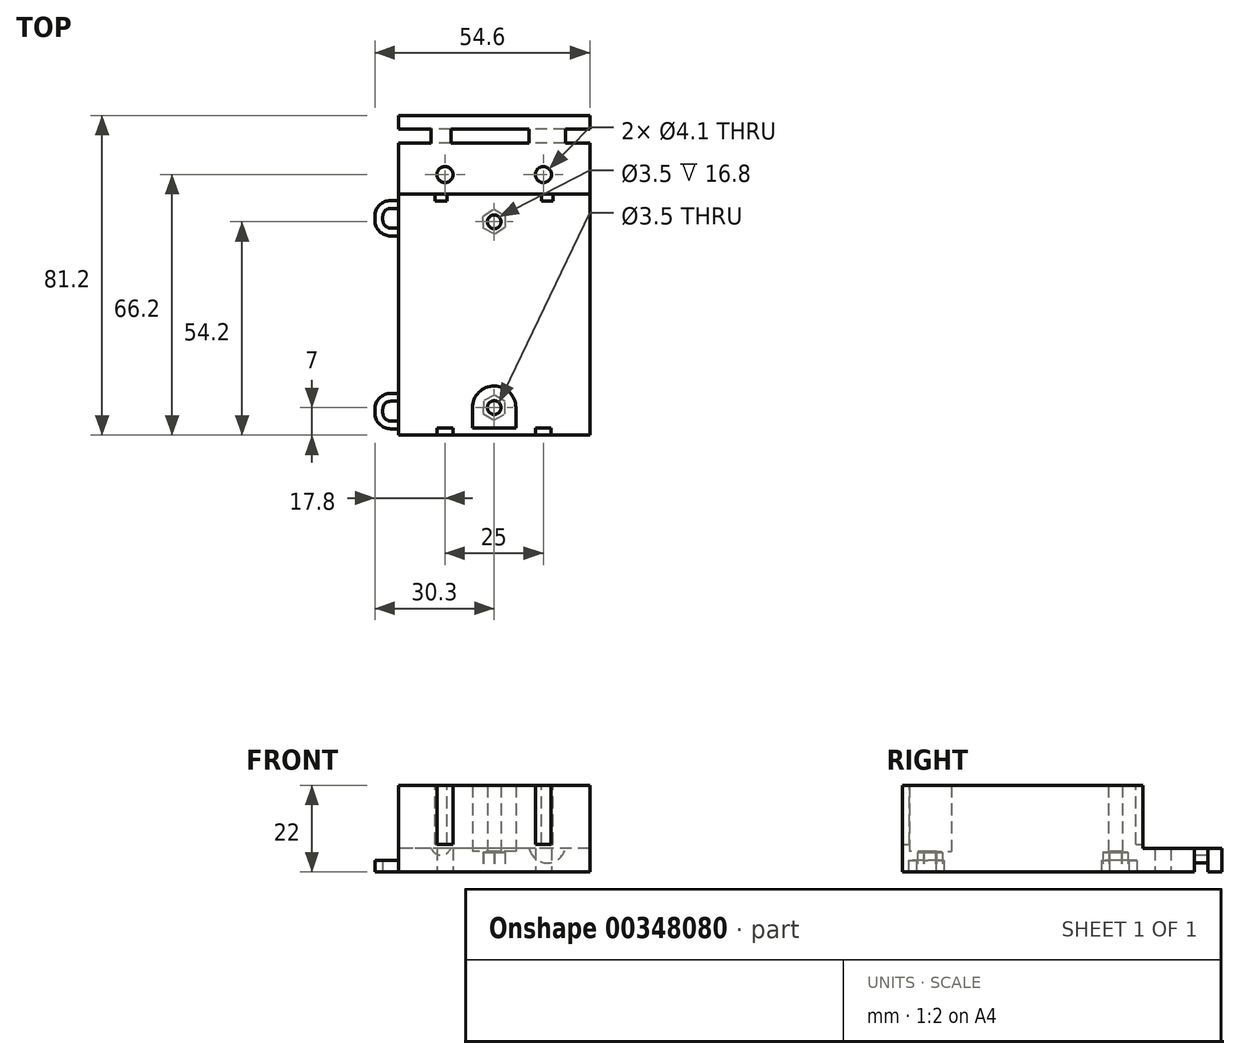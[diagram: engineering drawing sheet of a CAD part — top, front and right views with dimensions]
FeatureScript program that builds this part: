
annotation { "Feature Type Name" : "Feature", "Feature Type Description" : "" }
export const myFeature = defineFeature(function(context is Context, id is Id, definition is map)
    precondition{}
    {
        {
            var Q0;
            Q0=qCreatedBy(makeId("Top.planeOp"),FACE);
            var sketch = newSketch(context, id + "F0", { "sketchPlane" : qUnion([Q0])});
            skLineSegment(sketch, "E0.bottom", {"start": v(22.5, -28.8) * mm, "end": v(-22.5, -28.8) * mm});
            skLineSegment(sketch, "E0.top", {"start": v(22.5, 28.8) * mm, "end": v(-22.5, 28.8) * mm});
            skLineSegment(sketch, "E0.left", {"start": v(22.5, -28.8) * mm, "end": v(22.5, 28.8) * mm});
            skLineSegment(sketch, "E0.right", {"start": v(-22.5, -28.8) * mm, "end": v(-22.5, 28.8) * mm});
            skPoint(sketch, "E0.middle", {"position": v(0, 0) * mm});
            skLineSegment(sketch, "E1.bottom", {"start": v(24.3, -30.6) * mm, "end": v(-24.3, -30.6) * mm});
            skLineSegment(sketch, "E1.top", {"start": v(24.3, 50.6) * mm, "end": v(-24.3, 50.6) * mm});
            skLineSegment(sketch, "E1.left", {"start": v(24.3, -30.6) * mm, "end": v(24.3, 50.6) * mm});
            skLineSegment(sketch, "E1.right", {"start": v(-24.3, -30.6) * mm, "end": v(-24.3, 50.6) * mm});
            skPoint(sketch, "E1.middle", {"position": v(0, 10) * mm});
            skLineSegment(sketch, "E2", {"start": v(-24.3, 30.6) * mm, "end": v(24.3, 30.6) * mm});
            skPoint(sketch, "E3.startSnap0", {"position": v(-22.5, 0) * mm});
            skPoint(sketch, "E3.endSnap0", {"position": v(22.5, 0) * mm});
            skLineSegment(sketch, "E4", {"start": v(0, -30.6) * mm, "end": v(0, 50.6) * mm, "construction": true});
            skCircle(sketch, "E5", {"center": v(-12.5, 35.6) * mm, "radius": 2.05 * mm});
            skCircle(sketch, "E6.MirrorC", {"center": v(12.5, 35.6) * mm, "radius": 2.05 * mm});
            skCircle(sketch, "E7", {"center": v(0, 23.6) * mm, "radius": 1.75 * mm});
            skArc(sketch, "E8", {"start": v(-5.5, 23.6) * mm, "mid": v(0, 18.1) * mm, "end": v(5.5, 23.6) * mm});
            skLineSegment(sketch, "E9", {"start": v(-5.5, 23.6) * mm, "end": v(-5.5, 28.8) * mm});
            skLineSegment(sketch, "E10", {"start": v(5.5, 23.6) * mm, "end": v(5.5, 28.8) * mm});
            skLineSegment(sketch, "E11", {"start": v(-22.5, 0) * mm, "end": v(22.5, 0) * mm, "construction": true});
            skArc(sketch, "E12.MirrorCS", {"start": v(-5.5, -23.6) * mm, "mid": v(0, -18.1) * mm, "end": v(5.5, -23.6) * mm});
            skCircle(sketch, "E13.MirrorC", {"center": v(0, -23.6) * mm, "radius": 1.75 * mm});
            skLineSegment(sketch, "E14.MirrorCS", {"start": v(-5.5, -23.6) * mm, "end": v(-5.5, -28.8) * mm});
            skLineSegment(sketch, "E15.MirrorCS", {"start": v(5.5, -23.6) * mm, "end": v(5.5, -28.8) * mm});
            skSolve(sketch);
        }
        {
            var Q0;
            Q0=makeQuery(id+"F0.imprint","IMPRINT",FACE,{"disambiguationData":[TD([[makeQuery(id+"F0.imprint","IMPRINT",EDGE,{"derivedFrom":sQuery(id+"F0.wireOp",EDGE,"E0.bottom")}),1.0]])]});
            extrude(context, id + "F1", {"entities" : qUnion([Q0]), "depth" : 22 * mm});
        }
        {
            var Q0;
            Q0=makeQuery(id+"F0.imprint","IMPRINT",FACE,{"disambiguationData":[TD([[makeQuery(id+"F0.imprint","IMPRINT",EDGE,{"derivedFrom":sQuery(id+"F0.wireOp",EDGE,"E12.MirrorCS")}),-1.0]])]});
            var Q1;
            Q1=makeQuery(id+"F0.imprint","IMPRINT",FACE,{"disambiguationData":[TD([[makeQuery(id+"F0.imprint","IMPRINT",EDGE,{"derivedFrom":sQuery(id+"F0.wireOp",EDGE,"E7")}),-1.0]])]});
            extrude(context, id + "F2", {"entities" : qUnion([Q0, Q1]), "operationType" : NewBodyOperationType.ADD, "depth" : 22 * mm});
        }
        {
            var Q0;
            Q0=makeQuery(id+"F0.imprint","IMPRINT",FACE,{"disambiguationData":[TD([[makeQuery(id+"F0.imprint","IMPRINT",EDGE,{"derivedFrom":sQuery(id+"F0.wireOp",EDGE,"E0.bottom")}),-1.0]])]});
            extrude(context, id + "F3", {"entities" : qUnion([Q0]), "operationType" : NewBodyOperationType.ADD, "depth" : 1 * mm});
        }
        {
            var Q0;
            {var subQ2=sQuery(id+"F0.wireOp",EDGE,"E1.top");Q0=makeQuery(id+"F0.imprint","IMPRINT",FACE,{"disambiguationData":[TD([[makeQuery(id+"F0.imprint","IMPRINT",EDGE,{"derivedFrom":subQ2}),1.0]])]});}
            extrude(context, id + "F4", {"entities" : qUnion([Q0]), "operationType" : NewBodyOperationType.ADD, "depth" : 6 * mm});
        }
        {
            var Q0;
            Q0=makeQuery(id+"F1.opExtrude","CAP_FACE",FACE,{"disambiguationData":[OSD([sQuery(id+"F0.wireOp",EDGE,"E0.bottom"),sQuery(id+"F0.wireOp",EDGE,"E0.top"),sQuery(id+"F0.wireOp",EDGE,"E0.left"),sQuery(id+"F0.wireOp",EDGE,"E0.right"),sQuery(id+"F0.wireOp",EDGE,"E1.bottom"),sQuery(id+"F0.wireOp",EDGE,"E1.left"),sQuery(id+"F0.wireOp",EDGE,"E1.right"),sQuery(id+"F0.wireOp",EDGE,"E2"),sQuery(id+"F0.wireOp",EDGE,"yR1164SM-HHxc-F0gP-5n0t-cE52RilRuhD8"),sQuery(id+"F0.wireOp",EDGE,"339f27e5-fe4a-4800-860f-37246a4f3ca70.MirrorC"),sQuery(id+"F0.wireOp",EDGE,"269baa23-9682-4f4a-8466-03d9806e97a70.MirrorC"),sQuery(id+"F0.wireOp",EDGE,"ced02980-3db4-49ca-8f9b-05a1ab2736510.MirrorC")])],"isStart":false});
            var sketch = newSketch(context, id + "F5", { "sketchPlane" : qUnion([Q0])});
            skLineSegment(sketch, "E16.bottom", {"start": v(-12, 28.8) * mm, "end": v(-15, 28.8) * mm});
            skLineSegment(sketch, "E16.top", {"start": v(-12, 30.6) * mm, "end": v(-15, 30.6) * mm});
            skLineSegment(sketch, "E16.left", {"start": v(-12, 28.8) * mm, "end": v(-12, 30.6) * mm});
            skLineSegment(sketch, "E16.right", {"start": v(-15, 28.8) * mm, "end": v(-15, 30.6) * mm});
            skPoint(sketch, "E16.middle", {"position": v(-13.5, 29.7) * mm});
            skLineSegment(sketch, "E17.MirrorCS", {"start": v(12, 28.8) * mm, "end": v(12, 30.6) * mm});
            skLineSegment(sketch, "E18.MirrorCS", {"start": v(12, 28.8) * mm, "end": v(15, 28.8) * mm});
            skLineSegment(sketch, "E19.MirrorCS", {"start": v(15, 28.8) * mm, "end": v(15, 30.6) * mm});
            skLineSegment(sketch, "E20.MirrorCS", {"start": v(12, 30.6) * mm, "end": v(15, 30.6) * mm});
            skLineSegment(sketch, "E21.bottom", {"start": v(-10.5, -30.6) * mm, "end": v(-14.5, -30.6) * mm});
            skLineSegment(sketch, "E21.top", {"start": v(-10.5, -28.8) * mm, "end": v(-14.5, -28.8) * mm});
            skLineSegment(sketch, "E21.left", {"start": v(-10.5, -30.6) * mm, "end": v(-10.5, -28.8) * mm});
            skLineSegment(sketch, "E21.right", {"start": v(-14.5, -30.6) * mm, "end": v(-14.5, -28.8) * mm});
            skPoint(sketch, "E21.middle", {"position": v(-12.5, -29.7) * mm});
            skLineSegment(sketch, "E22.MirrorCS", {"start": v(10.5, -30.6) * mm, "end": v(10.5, -28.8) * mm});
            skLineSegment(sketch, "E23.MirrorCS", {"start": v(10.5, -28.8) * mm, "end": v(14.5, -28.8) * mm});
            skLineSegment(sketch, "E24.MirrorCS", {"start": v(10.5, -30.6) * mm, "end": v(14.5, -30.6) * mm});
            skLineSegment(sketch, "E25.MirrorCS", {"start": v(14.5, -30.6) * mm, "end": v(14.5, -28.8) * mm});
            skSolve(sketch);
        }
        {
            var Q0;
            Q0=qSketchRegion(id+"F5",true);
            extrude(context, id + "F6", {"entities" : qUnion([Q0]), "operationType" : NewBodyOperationType.REMOVE, "oppositeDirection" : true, "depth" : 15 * mm});
        }
        {
            var Q0;
            Q0=makeQuery(id+"F4.opExtrude","SWEPT_FACE",FACE,{"disambiguationData":[OSD([sQuery(id+"F0.wireOp",EDGE,"E1.top")])]});
            var sketch = newSketch(context, id + "F7", { "sketchPlane" : qUnion([Q0])});
            skPoint(sketch, "E26.0", {"position": v(13.5, 7) * mm});
            skLineSegment(sketch, "E27", {"start": v(0, 0) * mm, "end": v(0, 22.29) * mm, "construction": true});
            skPoint(sketch, "E27.endSnap0", {"position": v(0, 0) * mm});
            skLineSegment(sketch, "E28.0", {"start": v(-24.3, 6) * mm, "end": v(24.3, 6) * mm});
            skArc(sketch, "E29", {"start": v(11, 6) * mm, "mid": v(13.5, 4.3) * mm, "end": v(16, 6) * mm});
            skArc(sketch, "E30.0", {"start": v(8.92, 6) * mm, "mid": v(13.5, 2.3) * mm, "end": v(18.08, 6) * mm});
            skArc(sketch, "E31.MirrorCS", {"start": v(-8.92, 6) * mm, "mid": v(-13.5, 2.3) * mm, "end": v(-18.08, 6) * mm});
            skArc(sketch, "E32.MirrorCS", {"start": v(-11, 6) * mm, "mid": v(-13.5, 4.3) * mm, "end": v(-16, 6) * mm});
            skSolve(sketch);
        }
        {
            var Q0;
            {var subQ0=sQuery(id+"F7.wireOp",EDGE,"E29");Q0=makeQuery(id+"F7.imprint","IMPRINT",FACE,{"disambiguationData":[TD([[makeQuery(id+"F7.imprint","IMPRINT",EDGE,{"derivedFrom":subQ0}),-1.0]])]});}
            var Q1;
            {var subQ0=sQuery(id+"F7.wireOp",EDGE,"E31.MirrorCS");Q1=makeQuery(id+"F7.imprint","IMPRINT",FACE,{"disambiguationData":[TD([[makeQuery(id+"F7.imprint","IMPRINT",EDGE,{"derivedFrom":subQ0}),-1.0]])]});}
            extrude(context, id + "F8", {"entities" : qUnion([Q0, Q1]), "operationType" : NewBodyOperationType.REMOVE, "oppositeDirection" : true, "depth" : 7 * mm});
        }
        {
            var Q0;
            {var subQ0=sQuery(id+"F7.wireOp",EDGE,"E29");Q0=makeQuery(id+"F7.imprint","IMPRINT",FACE,{"disambiguationData":[TD([[makeQuery(id+"F7.imprint","IMPRINT",EDGE,{"derivedFrom":subQ0}),-1.0]])]});}
            var Q1;
            {var subQ0=sQuery(id+"F7.wireOp",EDGE,"E31.MirrorCS");Q1=makeQuery(id+"F7.imprint","IMPRINT",FACE,{"disambiguationData":[TD([[makeQuery(id+"F7.imprint","IMPRINT",EDGE,{"derivedFrom":subQ0}),-1.0]])]});}
            extrude(context, id + "F9", {"entities" : qUnion([Q0, Q1]), "operationType" : NewBodyOperationType.ADD, "oppositeDirection" : true, "depth" : (7 - 3.5) * mm});
        }
        {
            var Q0;
            {var subQ1=sQuery(id+"F0.wireOp",EDGE,"E0.left");Q0=makeQuery(id+"F0.imprint","IMPRINT",FACE,{"disambiguationData":[TD([[makeQuery(id+"F0.imprint","IMPRINT",EDGE,{"derivedFrom":subQ1}),1.0]])]});}
            var sketch = newSketch(context, id + "F10", { "sketchPlane" : qUnion([Q0])});
            skPoint(sketch, "E33.0", {"position": v(0, 23.6) * mm});
            skCircle(sketch, "E34.cCircle", {"center": v(0, 23.6) * mm, "radius": 2.75 * mm, "construction": true});
            skLineSegment(sketch, "E34.0", {"start": v(0.1, 20.43) * mm, "end": v(-2.7, 21.93) * mm});
            skLineSegment(sketch, "E34.1", {"start": v(-2.7, 21.93) * mm, "end": v(-2.8, 25.1) * mm});
            skLineSegment(sketch, "E34.2", {"start": v(-2.8, 25.1) * mm, "end": v(-0.1, 26.77) * mm});
            skLineSegment(sketch, "E34.3", {"start": v(-0.1, 26.77) * mm, "end": v(2.7, 25.27) * mm});
            skLineSegment(sketch, "E34.4", {"start": v(2.7, 25.27) * mm, "end": v(2.8, 22.1) * mm});
            skLineSegment(sketch, "E34.5", {"start": v(2.8, 22.1) * mm, "end": v(0.1, 20.43) * mm});
            skPoint(sketch, "E34.0.midPoint", {"position": v(-1.3, 21.18) * mm});
            skLineSegment(sketch, "E35.MirrorCS", {"start": v(2.8, -22.1) * mm, "end": v(0.1, -20.43) * mm});
            skLineSegment(sketch, "E36.MirrorCS", {"start": v(2.7, -25.27) * mm, "end": v(2.8, -22.1) * mm});
            skLineSegment(sketch, "E37.MirrorCS", {"start": v(-0.1, -26.77) * mm, "end": v(2.7, -25.27) * mm});
            skLineSegment(sketch, "E38.MirrorCS", {"start": v(-2.8, -25.1) * mm, "end": v(-0.1, -26.77) * mm});
            skLineSegment(sketch, "E39.MirrorCS", {"start": v(-2.7, -21.93) * mm, "end": v(-2.8, -25.1) * mm});
            skLineSegment(sketch, "E40.MirrorCS", {"start": v(0.1, -20.43) * mm, "end": v(-2.7, -21.93) * mm});
            skSolve(sketch);
        }
        {
            var Q0;
            Q0=makeQuery(id+"F0.imprint","IMPRINT",FACE,{"disambiguationData":[TD([[makeQuery(id+"F0.imprint","IMPRINT",EDGE,{"derivedFrom":sQuery(id+"F0.wireOp",EDGE,"E7")}),1.0]])]});
            var Q1;
            Q1=makeQuery(id+"F0.imprint","IMPRINT",FACE,{"disambiguationData":[TD([[makeQuery(id+"F0.imprint","IMPRINT",EDGE,{"derivedFrom":sQuery(id+"F0.wireOp",EDGE,"E13.MirrorC")}),-1.0]])]});
            extrude(context, id + "F11", {"entities" : qUnion([Q0, Q1]), "operationType" : NewBodyOperationType.ADD, "depth" : (5 + 0.2) * mm});
        }
        {
            var Q0;
            Q0=qSketchRegion(id+"F10",true);
            extrude(context, id + "F12", {"entities" : qUnion([Q0]), "operationType" : NewBodyOperationType.REMOVE, "depth" : 5 * mm});
        }
        {
            var Q0;
            {var subQ2=sQuery(id+"F0.wireOp",EDGE,"E1.top");Q0=makeQuery(id+"F0.imprint","IMPRINT",FACE,{"disambiguationData":[TD([[makeQuery(id+"F0.imprint","IMPRINT",EDGE,{"derivedFrom":subQ2}),1.0]])]});}
            var sketch = newSketch(context, id + "F13", { "sketchPlane" : qUnion([Q0])});
            skLineSegment(sketch, "E41.0", {"start": v(-24.3, -30.6) * mm, "end": v(-24.3, 50.6) * mm});
            skLineSegment(sketch, "E42.bottom", {"start": v(-24.3, 27) * mm, "end": v(-26.3, 27) * mm});
            skLineSegment(sketch, "E42.top", {"start": v(-24.3, 22) * mm, "end": v(-26.3, 22) * mm});
            skLineSegment(sketch, "E42.left", {"start": v(-24.3, 27) * mm, "end": v(-24.3, 22) * mm});
            skLineSegment(sketch, "E42.right", {"start": v(-28.3, 25) * mm, "end": v(-28.3, 24) * mm});
            skPoint(sketch, "E43.visualSharp", {"position": v(-28.3, 27) * mm});
            skArc(sketch, "E43.filletArc", {"start": v(-26.3, 27) * mm, "mid": v(-27.71, 26.41) * mm, "end": v(-28.3, 25) * mm});
            skPoint(sketch, "E44.visualSharp", {"position": v(-28.3, 22) * mm});
            skArc(sketch, "E44.filletArc", {"start": v(-28.3, 24) * mm, "mid": v(-27.71, 22.59) * mm, "end": v(-26.3, 22) * mm});
            skLineSegment(sketch, "E45.0", {"start": v(-24.3, 20) * mm, "end": v(-26.3, 20) * mm});
            skLineSegment(sketch, "E45.1", {"start": v(-24.3, 29) * mm, "end": v(-26.3, 29) * mm});
            skArc(sketch, "E45.2", {"start": v(-26.3, 29) * mm, "mid": v(-29.13, 27.83) * mm, "end": v(-30.3, 25) * mm});
            skLineSegment(sketch, "E45.3", {"start": v(-30.3, 25) * mm, "end": v(-30.3, 24) * mm});
            skArc(sketch, "E45.4", {"start": v(-30.3, 24) * mm, "mid": v(-29.13, 21.17) * mm, "end": v(-26.3, 20) * mm});
            skLineSegment(sketch, "E46", {"start": v(-24.3, 29) * mm, "end": v(-24.3, 20) * mm});
            skLineSegment(sketch, "E47.MirrorCS", {"start": v(-24.3, -20) * mm, "end": v(-26.3, -20) * mm});
            skArc(sketch, "E48.MirrorCS", {"start": v(-30.3, -24) * mm, "mid": v(-29.13, -21.17) * mm, "end": v(-26.3, -20) * mm});
            skLineSegment(sketch, "E49.MirrorCS", {"start": v(-30.3, -25) * mm, "end": v(-30.3, -24) * mm});
            skArc(sketch, "E50.MirrorCS", {"start": v(-26.3, -29) * mm, "mid": v(-29.13, -27.83) * mm, "end": v(-30.3, -25) * mm});
            skLineSegment(sketch, "E51.MirrorCS", {"start": v(-24.3, -29) * mm, "end": v(-26.3, -29) * mm});
            skLineSegment(sketch, "E52.MirrorCS", {"start": v(-24.3, -27) * mm, "end": v(-26.3, -27) * mm});
            skArc(sketch, "E53.MirrorCS", {"start": v(-26.3, -27) * mm, "mid": v(-27.71, -26.41) * mm, "end": v(-28.3, -25) * mm});
            skLineSegment(sketch, "E54.MirrorCS", {"start": v(-28.3, -25) * mm, "end": v(-28.3, -24) * mm});
            skArc(sketch, "E55.MirrorCS", {"start": v(-28.3, -24) * mm, "mid": v(-27.71, -22.59) * mm, "end": v(-26.3, -22) * mm});
            skLineSegment(sketch, "E56.MirrorCS", {"start": v(-24.3, -22) * mm, "end": v(-26.3, -22) * mm});
            skSolve(sketch);
        }
        {
            var Q0;
            {var subQ1=sQuery(id+"F13.wireOp",EDGE,"E47.MirrorCS");Q0=makeQuery(id+"F13.imprint","IMPRINT",FACE,{"disambiguationData":[TD([[makeQuery(id+"F13.imprint","IMPRINT",EDGE,{"derivedFrom":subQ1}),1.0]])]});}
            var Q1;
            {var subQ2=sQuery(id+"F13.wireOp",EDGE,"E42.bottom");Q1=makeQuery(id+"F13.imprint","IMPRINT",FACE,{"disambiguationData":[TD([[makeQuery(id+"F13.imprint","IMPRINT",EDGE,{"derivedFrom":subQ2}),-1.0]])]});}
            extrude(context, id + "F14", {"entities" : qUnion([Q0, Q1]), "operationType" : NewBodyOperationType.ADD, "depth" : 3 * mm});
        }
    });
